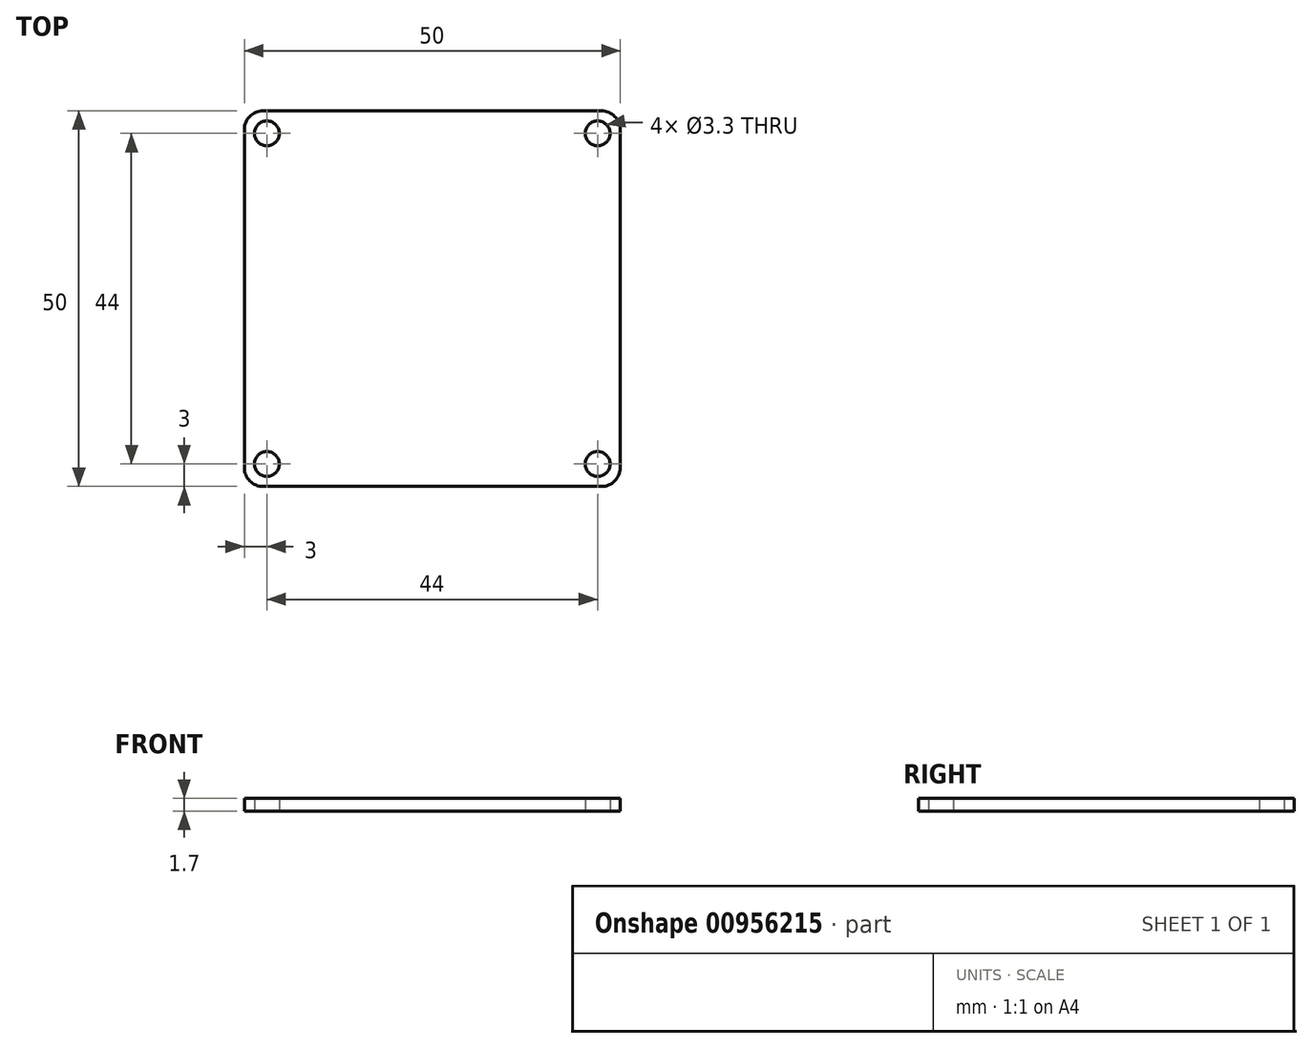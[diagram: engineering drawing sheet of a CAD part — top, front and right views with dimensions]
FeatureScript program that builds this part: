
annotation { "Feature Type Name" : "Feature", "Feature Type Description" : "" }
export const myFeature = defineFeature(function(context is Context, id is Id, definition is map)
    precondition{}
    {
        {
            var Q0;
            Q0=qCreatedBy(makeId("Top.planeOp"),FACE);
            var sketch = newSketch(context, id + "F0", { "sketchPlane" : qUnion([Q0])});
            skLineSegment(sketch, "E0.bottom", {"start": v(22.5, 25) * mm, "end": v(-22.5, 25) * mm});
            skLineSegment(sketch, "E0.top", {"start": v(22.5, -25) * mm, "end": v(-22.5, -25) * mm});
            skLineSegment(sketch, "E0.left", {"start": v(25, 22.5) * mm, "end": v(25, -22.5) * mm});
            skLineSegment(sketch, "E0.right", {"start": v(-25, 22.5) * mm, "end": v(-25, -22.5) * mm});
            skPoint(sketch, "E0.middle", {"position": v(0, 0) * mm});
            skPoint(sketch, "E1.visualSharp", {"position": v(-25, 25) * mm});
            skArc(sketch, "E1.filletArc", {"start": v(-22.5, 25) * mm, "mid": v(-24.27, 24.27) * mm, "end": v(-25, 22.5) * mm});
            skPoint(sketch, "E2.visualSharp", {"position": v(25, 25) * mm});
            skArc(sketch, "E2.filletArc", {"start": v(25, 22.5) * mm, "mid": v(24.27, 24.27) * mm, "end": v(22.5, 25) * mm});
            skPoint(sketch, "E3.visualSharp", {"position": v(25, -25) * mm});
            skArc(sketch, "E3.filletArc", {"start": v(22.5, -25) * mm, "mid": v(24.27, -24.27) * mm, "end": v(25, -22.5) * mm});
            skPoint(sketch, "E4.visualSharp", {"position": v(-25, -25) * mm});
            skArc(sketch, "E4.filletArc", {"start": v(-25, -22.5) * mm, "mid": v(-24.27, -24.27) * mm, "end": v(-22.5, -25) * mm});
            skCircle(sketch, "E5", {"center": v(-22, 22) * mm, "radius": 1.65 * mm});
            skCircle(sketch, "E6.0.1.0", {"center": v(-22, -22) * mm, "radius": 1.65 * mm});
            skCircle(sketch, "E6.1.0.0", {"center": v(22, 22) * mm, "radius": 1.65 * mm});
            skCircle(sketch, "E6.1.1.0", {"center": v(22, -22) * mm, "radius": 1.65 * mm});
            skLineSegment(sketch, "E6.direction1", {"start": v(-22, 22) * mm, "end": v(22, 22) * mm, "construction": true});
            skLineSegment(sketch, "E6.direction2", {"start": v(-22, 22) * mm, "end": v(-22, -22) * mm, "construction": true});
            skCircle(sketch, "E7", {"center": v(0, 0) * mm, "radius": 5 * mm, "construction": true});
            skSolve(sketch);
        }
        {
            var Q0;
            Q0=makeQuery(id+"F0.imprint","IMPRINT",FACE,{"disambiguationData":[TD([[makeQuery(id+"F0.imprint","IMPRINT",EDGE,{"derivedFrom":sQuery(id+"F0.wireOp",EDGE,"E0.bottom")}),1.0]])]});
            extrude(context, id + "F1", {"entities" : qUnion([Q0]), "depth" : 1.7 * mm, "offsetDistance" : 25 * mm});
        }
    });
